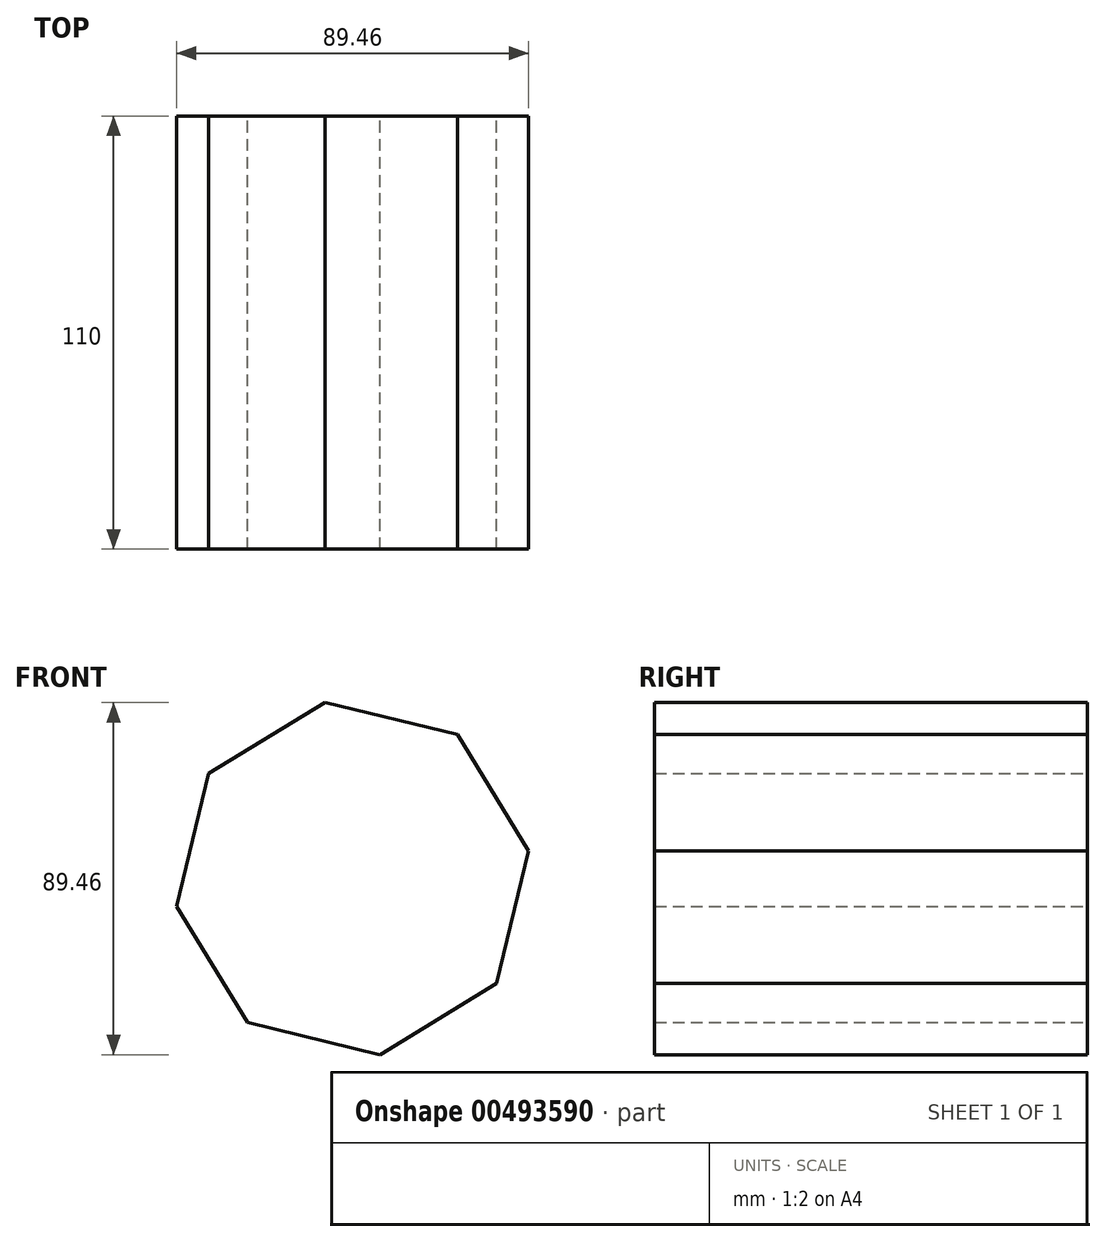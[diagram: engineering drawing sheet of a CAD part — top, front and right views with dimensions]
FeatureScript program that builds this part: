
annotation { "Feature Type Name" : "Feature", "Feature Type Description" : "" }
export const myFeature = defineFeature(function(context is Context, id is Id, definition is map)
    precondition{}
    {
        {
            var Q0;
            Q0=qCreatedBy(makeId("Front.planeOp"),FACE);
            var sketch = newSketch(context, id + "F0", { "sketchPlane" : qUnion([Q0])});
            skCircle(sketch, "E0.cCircle", {"center": v(0, 0) * mm, "radius": 45.27 * mm, "construction": true});
            skLineSegment(sketch, "E0.0", {"start": v(-26.68, -36.58) * mm, "end": v(-44.73, -7) * mm});
            skLineSegment(sketch, "E0.1", {"start": v(-44.73, -7) * mm, "end": v(-36.58, 26.68) * mm});
            skLineSegment(sketch, "E0.2", {"start": v(-36.58, 26.68) * mm, "end": v(-7, 44.73) * mm});
            skLineSegment(sketch, "E0.3", {"start": v(-7, 44.73) * mm, "end": v(26.68, 36.58) * mm});
            skLineSegment(sketch, "E0.4", {"start": v(26.68, 36.58) * mm, "end": v(44.73, 7) * mm});
            skLineSegment(sketch, "E0.5", {"start": v(44.73, 7) * mm, "end": v(36.58, -26.68) * mm});
            skLineSegment(sketch, "E0.6", {"start": v(36.58, -26.68) * mm, "end": v(7, -44.73) * mm});
            skLineSegment(sketch, "E0.7", {"start": v(7, -44.73) * mm, "end": v(-26.68, -36.58) * mm});
            skSolve(sketch);
        }
        {
            var Q0;
            Q0=makeQuery(id+"F0.imprint","IMPRINT",FACE,{"disambiguationData":[TD([[makeQuery(id+"F0.imprint","IMPRINT",EDGE,{"derivedFrom":sQuery(id+"F0.wireOp",EDGE,"E0.0")}),-1.0]])]});
            extrude(context, id + "F1", {"entities" : qUnion([Q0]), "endBound" : BoundingType.SYMMETRIC, "depth" : 110 * mm});
        }
    });
